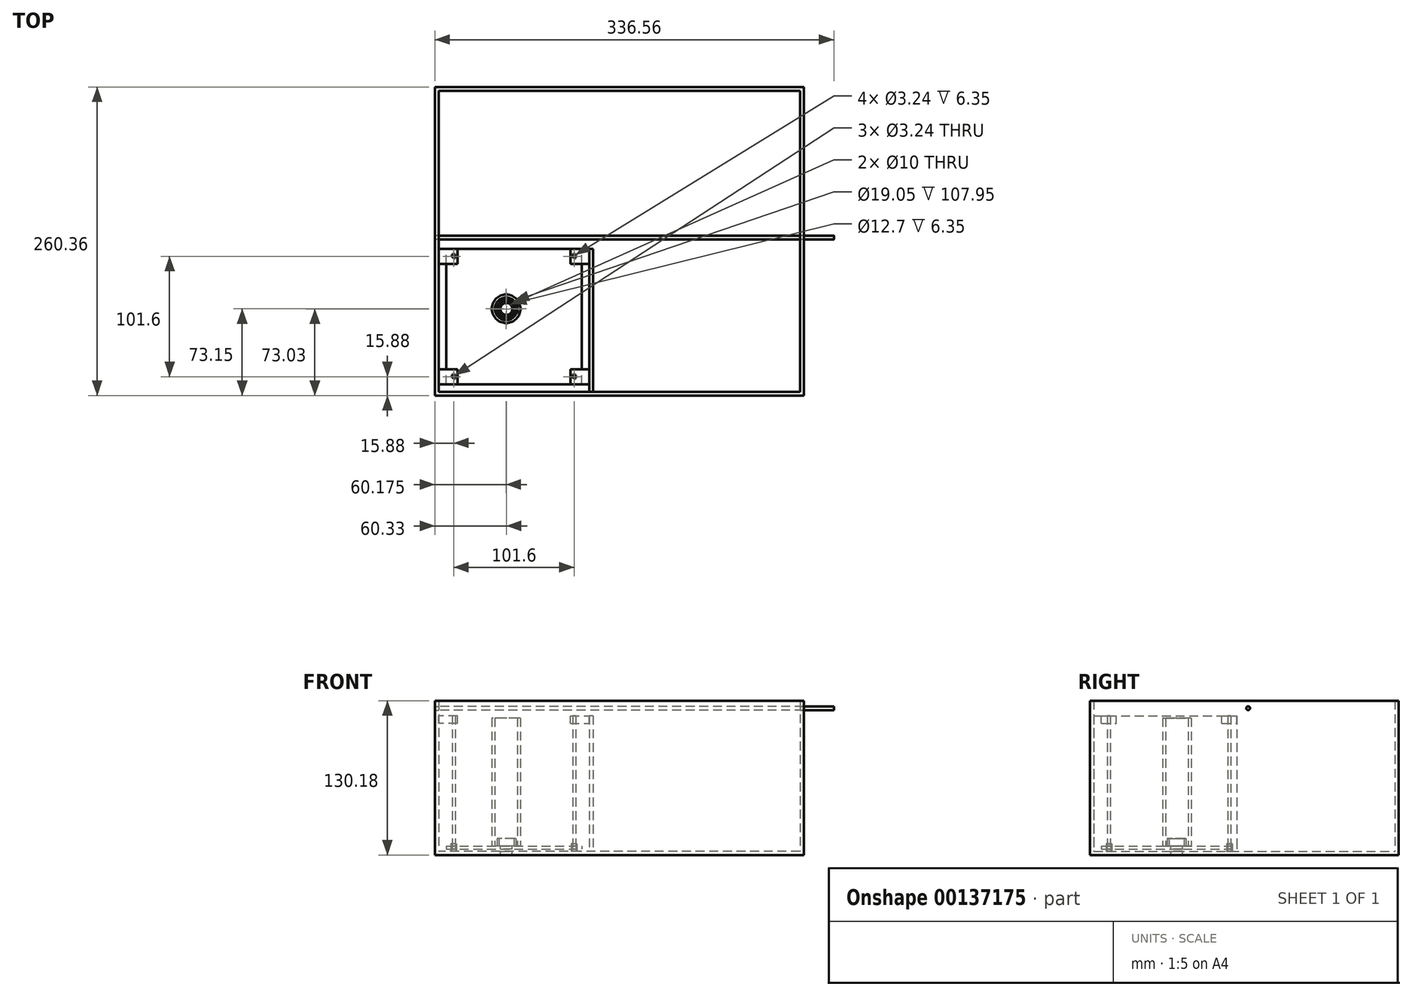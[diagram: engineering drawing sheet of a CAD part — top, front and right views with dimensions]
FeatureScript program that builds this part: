
annotation { "Feature Type Name" : "Feature", "Feature Type Description" : "" }
export const myFeature = defineFeature(function(context is Context, id is Id, definition is map)
    precondition{}
    {
        {
            var Q0;
            Q0=qCreatedBy(makeId("Top.planeOp"),FACE);
            var sketch = newSketch(context, id + "F0", { "sketchPlane" : qUnion([Q0])});
            skLineSegment(sketch, "E0.bottom", {"start": v(152.4, -127) * mm, "end": v(-152.4, -127) * mm});
            skLineSegment(sketch, "E0.top", {"start": v(152.4, 127) * mm, "end": v(-152.4, 127) * mm});
            skLineSegment(sketch, "E0.left", {"start": v(152.4, -127) * mm, "end": v(152.4, 127) * mm});
            skLineSegment(sketch, "E0.right", {"start": v(-152.4, -127) * mm, "end": v(-152.4, 127) * mm});
            skPoint(sketch, "E0.middle", {"position": v(0, 0) * mm});
            skLineSegment(sketch, "E1.0", {"start": v(155.58, 130.17) * mm, "end": v(-155.58, 130.17) * mm});
            skLineSegment(sketch, "E1.1", {"start": v(155.58, -130.18) * mm, "end": v(155.58, 130.17) * mm});
            skLineSegment(sketch, "E1.2", {"start": v(155.58, -130.18) * mm, "end": v(-155.58, -130.18) * mm});
            skLineSegment(sketch, "E1.3", {"start": v(-155.58, -130.18) * mm, "end": v(-155.58, 130.17) * mm});
            skSolve(sketch);
        }
        {
            var Q0;
            Q0 = qSketchRegion(id + "F0", true);
            extrude(context, id + "F1", {"entities" : qUnion([Q0]), "depth" : 127 * mm});
        }
        {
            var Q0;
            Q0=makeQuery(id+"F1.opExtrude","CAP_FACE",FACE,{"disambiguationData":[OSD([sQuery(id+"F0.wireOp",EDGE,"E0.bottom"),sQuery(id+"F0.wireOp",EDGE,"E0.top"),sQuery(id+"F0.wireOp",EDGE,"E0.left"),sQuery(id+"F0.wireOp",EDGE,"E0.right"),sQuery(id+"F0.wireOp",EDGE,"E1.0"),sQuery(id+"F0.wireOp",EDGE,"E1.1"),sQuery(id+"F0.wireOp",EDGE,"E1.2"),sQuery(id+"F0.wireOp",EDGE,"E1.3")])],"isStart":true});
            var sketch = newSketch(context, id + "F2", { "sketchPlane" : qUnion([Q0])});
            skLineSegment(sketch, "E2.0", {"start": v(-155.58, 130.18) * mm, "end": v(-155.58, -130.17) * mm});
            skLineSegment(sketch, "E3.0", {"start": v(155.58, -130.17) * mm, "end": v(-155.58, -130.17) * mm});
            skLineSegment(sketch, "E4.0", {"start": v(155.58, 130.18) * mm, "end": v(155.58, -130.17) * mm});
            skLineSegment(sketch, "E5.0", {"start": v(155.58, 130.18) * mm, "end": v(-155.58, 130.18) * mm});
            skSolve(sketch);
        }
        {
            var Q0;
            Q0 = qSketchRegion(id + "F2", true);
            extrude(context, id + "F3", {"entities" : qUnion([Q0]), "operationType" : NewBodyOperationType.ADD, "depth" : 3.17 * mm});
        }
        {
            var Q0;
            Q0=makeQuery(id+"F3.opExtrude","CAP_FACE",FACE,{"disambiguationData":[OSD([sQuery(id+"F2.wireOp",EDGE,"E2.0"),sQuery(id+"F2.wireOp",EDGE,"E3.0"),sQuery(id+"F2.wireOp",EDGE,"E4.0"),sQuery(id+"F2.wireOp",EDGE,"E5.0")])],"isStart":true});
            var sketch = newSketch(context, id + "F4", { "sketchPlane" : qUnion([Q0])});
            skLineSegment(sketch, "E6.bottom", {"start": v(-139.7, -114.3) * mm, "end": v(-38.1, -114.3) * mm, "construction": true});
            skLineSegment(sketch, "E6.top", {"start": v(-139.7, -12.7) * mm, "end": v(-38.1, -12.7) * mm, "construction": true});
            skLineSegment(sketch, "E6.left", {"start": v(-139.7, -114.3) * mm, "end": v(-139.7, -12.7) * mm, "construction": true});
            skLineSegment(sketch, "E6.right", {"start": v(-38.1, -114.3) * mm, "end": v(-38.1, -12.7) * mm, "construction": true});
            skCircle(sketch, "E7", {"center": v(-139.7, -114.3) * mm, "radius": 1.27 * mm});
            skCircle(sketch, "E8", {"center": v(-38.1, -114.3) * mm, "radius": 1.27 * mm});
            skCircle(sketch, "E9", {"center": v(-139.7, -12.7) * mm, "radius": 1.27 * mm});
            skCircle(sketch, "E10", {"center": v(-38.1, -12.7) * mm, "radius": 1.27 * mm});
            skSolve(sketch);
        }
        {
            var Q0;
            Q0 = qSketchRegion(id + "F4", true);
            extrude(context, id + "F5", {"entities" : qUnion([Q0]), "depth" : 114.3 * mm});
        }
        {
            var Q0;
            Q0=makeQuery(id+"F5.opExtrude","CAP_FACE",FACE,{"disambiguationData":[OSD([sQuery(id+"F4.wireOp",EDGE,"E9")])],"isStart":false});
            var sketch = newSketch(context, id + "F6", { "sketchPlane" : qUnion([Q0])});
            skPoint(sketch, "E11", {"position": v(-139.7, -12.7) * mm});
            skLineSegment(sketch, "E12.bottom", {"start": v(-136.53, -19.05) * mm, "end": v(-152.4, -19.05) * mm});
            skLineSegment(sketch, "E12.top", {"start": v(-136.53, -6.35) * mm, "end": v(-152.4, -6.35) * mm});
            skLineSegment(sketch, "E12.left", {"start": v(-136.53, -19.05) * mm, "end": v(-136.53, -6.35) * mm});
            skLineSegment(sketch, "E12.right", {"start": v(-152.4, -19.05) * mm, "end": v(-152.4, -6.35) * mm});
            skPoint(sketch, "E12.middle", {"position": v(-144.46, -12.7) * mm});
            skPoint(sketch, "E13", {"position": v(-139.7, -114.3) * mm});
            skLineSegment(sketch, "E14.bottom", {"start": v(-136.53, -120.65) * mm, "end": v(-152.4, -120.65) * mm});
            skLineSegment(sketch, "E14.top", {"start": v(-136.53, -107.95) * mm, "end": v(-152.4, -107.95) * mm});
            skLineSegment(sketch, "E14.left", {"start": v(-136.53, -120.65) * mm, "end": v(-136.53, -107.95) * mm});
            skLineSegment(sketch, "E14.right", {"start": v(-152.4, -120.65) * mm, "end": v(-152.4, -107.95) * mm});
            skPoint(sketch, "E14.middle", {"position": v(-144.46, -114.3) * mm});
            skSolve(sketch);
        }
        {
            var Q0;
            Q0 = qSketchRegion(id + "F6", true);
            extrude(context, id + "F7", {"entities" : qUnion([Q0]), "oppositeDirection" : true, "depth" : 6.35 * mm});
        }
        {
            var Q0;
            Q0=makeQuery(id+"F5.opExtrude","CAP_FACE",FACE,{"disambiguationData":[OSD([sQuery(id+"F4.wireOp",EDGE,"E7")])],"isStart":false});
            var sketch = newSketch(context, id + "F8", { "sketchPlane" : qUnion([Q0])});
            skPoint(sketch, "E15", {"position": v(-139.7, -114.3) * mm});
            skPoint(sketch, "E16", {"position": v(-38.1, -114.3) * mm});
            skSolve(sketch);
        }
        {
            var Q0;
            Q0=sQuery(id+"F8.wireOp",VERTEX,"E15");
            var Q1;
            Q1=sQuery(id+"F8.wireOp",VERTEX,"E16");
            cPlane(context, id + "F9", {"entities" : qUnion([Q0, Q1]), "cplaneType" : CPlaneType.MID_PLANE, "offset" : 25.4 * mm, "width" : 152.4 * mm, "height" : 152.4 * mm});
        }
        {
            var Q0;
            Q0=makeQuery(id+"F7.opExtrude","SWEPT_BODY",BODY,{"disambiguationData":[OSD([sQuery(id+"F6.wireOp",EDGE,"E12.bottom"),sQuery(id+"F6.wireOp",EDGE,"E12.top"),sQuery(id+"F6.wireOp",EDGE,"E12.left"),sQuery(id+"F6.wireOp",EDGE,"E12.right")])]});
            var Q1;
            Q1=makeQuery(id+"F7.opExtrude","SWEPT_BODY",BODY,{"disambiguationData":[OSD([sQuery(id+"F6.wireOp",EDGE,"E14.bottom"),sQuery(id+"F6.wireOp",EDGE,"E14.top"),sQuery(id+"F6.wireOp",EDGE,"E14.left"),sQuery(id+"F6.wireOp",EDGE,"E14.right")])]});
            var Q2;
            Q2=qCreatedBy(id+"F9.planeOp",FACE);
            mirror(context, id + "F10", {"entities" : qUnion([Q0, Q1]), "mirrorPlane" : qUnion([Q2])});
        }
        {
            var Q0;
            Q0=makeQuery(id+"F10.opPattern","COPY",FACE,{"derivedFrom":makeQuery(id+"F7.opExtrude","SWEPT_FACE",FACE,{"disambiguationData":[OSD([sQuery(id+"F6.wireOp",EDGE,"E12.right")])]}),"instanceName":"1"});
            var sketch = newSketch(context, id + "F11", { "sketchPlane" : qUnion([Q0])});
            skLineSegment(sketch, "E17.bottom", {"start": v(-127, 114.3) * mm, "end": v(-6.35, 114.3) * mm});
            skLineSegment(sketch, "E17.top", {"start": v(-127, 0) * mm, "end": v(-6.35, 0) * mm});
            skLineSegment(sketch, "E17.left", {"start": v(-127, 114.3) * mm, "end": v(-127, 0) * mm});
            skLineSegment(sketch, "E17.right", {"start": v(-6.35, 114.3) * mm, "end": v(-6.35, 0) * mm});
            skSolve(sketch);
        }
        {
            var Q0;
            Q0 = qSketchRegion(id + "F11", true);
            extrude(context, id + "F12", {"entities" : qUnion([Q0]), "depth" : 3.17 * mm});
        }
        {
            var Q0;
            Q0=makeQuery(id+"F3.opExtrude","CAP_FACE",FACE,{"disambiguationData":[OSD([sQuery(id+"F2.wireOp",EDGE,"E2.0"),sQuery(id+"F2.wireOp",EDGE,"E3.0"),sQuery(id+"F2.wireOp",EDGE,"E4.0"),sQuery(id+"F2.wireOp",EDGE,"E5.0")])],"isStart":true});
            var sketch = newSketch(context, id + "F13", { "sketchPlane" : qUnion([Q0])});
            skCircle(sketch, "E18", {"center": v(-139.7, -12.7) * mm, "radius": 2.38 * mm});
            skCircle(sketch, "E19", {"center": v(-139.7, -12.7) * mm, "radius": 1.62 * mm});
            skCircle(sketch, "E20", {"center": v(-38.1, -12.7) * mm, "radius": 1.62 * mm});
            skCircle(sketch, "E21", {"center": v(-38.1, -12.7) * mm, "radius": 2.38 * mm});
            skCircle(sketch, "E22", {"center": v(-139.7, -114.3) * mm, "radius": 1.62 * mm});
            skCircle(sketch, "E23", {"center": v(-139.7, -114.3) * mm, "radius": 2.38 * mm});
            skCircle(sketch, "E24", {"center": v(-38.1, -114.3) * mm, "radius": 1.62 * mm});
            skCircle(sketch, "E25", {"center": v(-38.1, -114.3) * mm, "radius": 2.38 * mm});
            skSolve(sketch);
        }
        {
            var Q0;
            Q0 = qSketchRegion(id + "F13", true);
            extrude(context, id + "F14", {"entities" : qUnion([Q0]), "depth" : 6.35 * mm});
        }
        {
            var Q0;
            Q0=makeQuery(id+"F14.opExtrude","CAP_FACE",FACE,{"disambiguationData":[OSD([sQuery(id+"F13.wireOp",EDGE,"E18"),sQuery(id+"F13.wireOp",EDGE,"E19")])],"isStart":false});
            var Q1;
            Q1=makeQuery(id+"F3.opExtrude","CAP_FACE",FACE,{"disambiguationData":[OSD([sQuery(id+"F2.wireOp",EDGE,"E2.0"),sQuery(id+"F2.wireOp",EDGE,"E3.0"),sQuery(id+"F2.wireOp",EDGE,"E4.0"),sQuery(id+"F2.wireOp",EDGE,"E5.0")])],"isStart":true});
            cPlane(context, id + "F15", {"entities" : qUnion([Q0, Q1]), "cplaneType" : CPlaneType.MID_PLANE, "offset" : 25.4 * mm, "width" : 152.4 * mm, "height" : 152.4 * mm});
        }
        {
            var Q0;
            Q0=qCreatedBy(id+"F15.planeOp",FACE);
            var sketch = newSketch(context, id + "F16", { "sketchPlane" : qUnion([Q0])});
            skLineSegment(sketch, "E26", {"start": v(-139.7, -12.7) * mm, "end": v(-38.1, -114.3) * mm, "construction": true});
            skLineSegment(sketch, "E27.bottom", {"start": v(-146.05, -120.65) * mm, "end": v(-31.75, -120.65) * mm});
            skLineSegment(sketch, "E27.top", {"start": v(-146.05, -6.35) * mm, "end": v(-31.75, -6.35) * mm});
            skLineSegment(sketch, "E27.left", {"start": v(-146.05, -120.65) * mm, "end": v(-146.05, -6.35) * mm});
            skLineSegment(sketch, "E27.right", {"start": v(-31.75, -120.65) * mm, "end": v(-31.75, -6.35) * mm});
            skPoint(sketch, "E27.middle", {"position": v(-88.9, -63.5) * mm});
            skCircle(sketch, "E28.0", {"center": v(-139.7, -12.7) * mm, "radius": 1.27 * mm});
            skCircle(sketch, "E29.0", {"center": v(-38.1, -12.7) * mm, "radius": 1.62 * mm});
            skCircle(sketch, "E30.0", {"center": v(-38.1, -114.3) * mm, "radius": 1.62 * mm});
            skCircle(sketch, "E31.0", {"center": v(-139.7, -114.3) * mm, "radius": 1.62 * mm});
            skSolve(sketch);
        }
        {
            var Q0;
            Q0 = qSketchRegion(id + "F16", true);
            extrude(context, id + "F17", {"entities" : qUnion([Q0]), "endBound" : BoundingType.SYMMETRIC, "depth" : 2.54 * mm});
        }
        {
            var Q0;
            Q0=makeQuery(id+"F3.boolean.opBoolean","MERGE",FACE,{"derivedFrom":[makeQuery(id+"F1.opExtrude","SWEPT_FACE",FACE,{"disambiguationData":[OSD([sQuery(id+"F0.wireOp",EDGE,"E1.1")])]}),makeQuery(id+"F3.opExtrude","SWEPT_FACE",FACE,{"disambiguationData":[OSD([sQuery(id+"F2.wireOp",EDGE,"E4.0")])]})]});
            var sketch = newSketch(context, id + "F18", { "sketchPlane" : qUnion([Q0])});
            skCircle(sketch, "E32", {"center": v(3.17, 120.65) * mm, "radius": 1.59 * mm});
            skSolve(sketch);
        }
        {
            var Q0;
            Q0 = qSketchRegion(id + "F18", true);
            extrude(context, id + "F19", {"entities" : qUnion([Q0]), "operationType" : NewBodyOperationType.REMOVE, "endBound" : BoundingType.THROUGH_ALL, "oppositeDirection" : true, "depth" : 25.4 * mm});
        }
        {
            var Q0;
            Q0=makeQuery(id+"F3.boolean.opBoolean","MERGE",FACE,{"derivedFrom":[makeQuery(id+"F1.opExtrude","SWEPT_FACE",FACE,{"disambiguationData":[OSD([sQuery(id+"F0.wireOp",EDGE,"E1.1")])]}),makeQuery(id+"F3.opExtrude","SWEPT_FACE",FACE,{"disambiguationData":[OSD([sQuery(id+"F2.wireOp",EDGE,"E4.0")])]})]});
            var sketch = newSketch(context, id + "F20", { "sketchPlane" : qUnion([Q0])});
            skCircle(sketch, "E33.0", {"center": v(3.17, 120.65) * mm, "radius": 1.59 * mm});
            skSolve(sketch);
        }
        {
            var Q0;
            Q0 = qSketchRegion(id + "F20", true);
            var Q1;
            Q1=makeQuery(id+"F3.boolean.opBoolean","MERGE",FACE,{"derivedFrom":[makeQuery(id+"F1.opExtrude","SWEPT_FACE",FACE,{"disambiguationData":[OSD([sQuery(id+"F0.wireOp",EDGE,"E1.3")])]}),makeQuery(id+"F3.opExtrude","SWEPT_FACE",FACE,{"disambiguationData":[OSD([sQuery(id+"F2.wireOp",EDGE,"E2.0")])]})]});
            extrude(context, id + "F21", {"entities" : qUnion([Q0]), "depth" : 25.4 * mm, "hasSecondDirection" : true, "secondDirectionBound" : SecondDirectionBoundingType.UP_TO_SURFACE, "secondDirectionOppositeDirection" : true, "secondDirectionBoundEntityFace" : qUnion([Q1]), "secondDirectionDepth" : 25.4 * mm});
        }
        {
            var Q0;
            Q0=makeQuery(id+"F17.opExtrude","CAP_FACE",FACE,{"disambiguationData":[OSD([sQuery(id+"F16.wireOp",EDGE,"E27.bottom"),sQuery(id+"F16.wireOp",EDGE,"E27.top"),sQuery(id+"F16.wireOp",EDGE,"E27.left"),sQuery(id+"F16.wireOp",EDGE,"E27.right"),sQuery(id+"F16.wireOp",EDGE,"E28.0"),sQuery(id+"F16.wireOp",EDGE,"E29.0"),sQuery(id+"F16.wireOp",EDGE,"E30.0"),sQuery(id+"F16.wireOp",EDGE,"E31.0")])],"isStart":false});
            var sketch = newSketch(context, id + "F22", { "sketchPlane" : qUnion([Q0])});
            skCircle(sketch, "E34", {"center": v(-95.25, -57.15) * mm, "radius": 7.94 * mm});
            skCircle(sketch, "E35", {"center": v(-95.25, -57.15) * mm, "radius": 6.35 * mm});
            skSolve(sketch);
        }
        {
            var Q0;
            Q0 = qSketchRegion(id + "F22", true);
            extrude(context, id + "F23", {"entities" : qUnion([Q0]), "depth" : 6.35 * mm});
        }
        {
            var Q0;
            Q0=makeQuery(id+"F17.opExtrude","CAP_FACE",FACE,{"disambiguationData":[OSD([sQuery(id+"F16.wireOp",EDGE,"E27.bottom"),sQuery(id+"F16.wireOp",EDGE,"E27.top"),sQuery(id+"F16.wireOp",EDGE,"E27.left"),sQuery(id+"F16.wireOp",EDGE,"E27.right"),sQuery(id+"F16.wireOp",EDGE,"E28.0"),sQuery(id+"F16.wireOp",EDGE,"E29.0"),sQuery(id+"F16.wireOp",EDGE,"E30.0"),sQuery(id+"F16.wireOp",EDGE,"E31.0")])],"isStart":false});
            var sketch = newSketch(context, id + "F24", { "sketchPlane" : qUnion([Q0])});
            skCircle(sketch, "E36", {"center": v(-95.4, -57.03) * mm, "radius": 12.07 * mm});
            skCircle(sketch, "E37", {"center": v(-95.4, -57.03) * mm, "radius": 9.53 * mm});
            skSolve(sketch);
        }
        {
            var Q0;
            Q0 = qSketchRegion(id + "F24", true);
            extrude(context, id + "F25", {"entities" : qUnion([Q0]), "depth" : 107.95 * mm});
        }
        {
            var Q0;
            Q0=makeQuery(id+"F17.opExtrude","CAP_FACE",FACE,{"disambiguationData":[OSD([sQuery(id+"F16.wireOp",EDGE,"E27.bottom"),sQuery(id+"F16.wireOp",EDGE,"E27.top"),sQuery(id+"F16.wireOp",EDGE,"E27.left"),sQuery(id+"F16.wireOp",EDGE,"E27.right"),sQuery(id+"F16.wireOp",EDGE,"E28.0"),sQuery(id+"F16.wireOp",EDGE,"E29.0"),sQuery(id+"F16.wireOp",EDGE,"E30.0"),sQuery(id+"F16.wireOp",EDGE,"E31.0")])],"isStart":false});
            var sketch = newSketch(context, id + "F26", { "sketchPlane" : qUnion([Q0])});
            skCircle(sketch, "E38", {"center": v(-95.25, -57.15) * mm, "radius": 5 * mm});
            skSolve(sketch);
        }
        {
            var Q0;
            Q0 = qSketchRegion(id + "F26", true);
            extrude(context, id + "F27", {"entities" : qUnion([Q0]), "operationType" : NewBodyOperationType.REMOVE, "endBound" : BoundingType.THROUGH_ALL, "oppositeDirection" : true, "depth" : 25.4 * mm});
        }
    });
